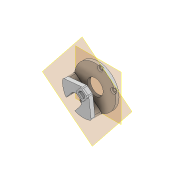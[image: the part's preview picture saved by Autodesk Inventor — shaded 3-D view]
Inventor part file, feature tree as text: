
AUTODESK INVENTOR PART (.ipt)
format: ipt  version: 2022 (Build 260153000, 153)  size: 436,224 bytes
history: native  units: in
note: dims shown in document units (in); Inventor stores cm internally (conversion verified against a paired STEP export)
features: sketch x8, extrude x7, reference x5, projected_geometry x5, other x4, plane x2, fillet x2, hole x1
ambient origin geometry x8: Origin, YZ Plane, XZ Plane, XY Plane, X Axis, Y Axis, Z Axis, Center Point
bodies: Solid1 (feature_tree), Volumenkörper2 (feature_tree)
feature tree (34):
  plane  "Work Plane1"
  extrude  "Extrusion1"  Depth=0.0787in
  hole  "Bohrung1"  [1 undecoded]
  extrude  "Extrusion4"  Depth=0.0787in
  plane  "Arbeitsebene2"
  extrude  "Extrusion6"  Depth=0.2756in TaperAngle=0.0deg
  fillet  "Rundung1"  Radius=0.2651in
  extrude  "Extrusion8"  Depth=0.0787in
  fillet  "Rundung2"  Radius=0.1969in
  extrude  "Extrusion9"  Depth=0.4331in TaperAngle=0.0deg
  extrude  "Extrusion10"  Depth=0.0787in
  extrude  "Extrusion11"  Depth=1.0236in
  sketch  "Sketch1"  dims[d0=0.1575in d1=0.0in]
  reference  "Reference1"
  reference  "Reference5"
  reference  "Reference6"
  reference  "Reference7"
  sketch  "Skizze4"  dims[d9=0.126in d10=0.75in d11=0.2559in d12=0.0787in d13=0.5635in d14=1.0in d15=0.8108in d17=0.7874in]
  reference  "Referenz9"
  sketch  "Skizze6"  dims[d18=0.5118in d19=0.3937in d20=0.0in]
  sketch  "Skizze10"  dims[d33=0.2756in d34=0.0in d37=0.0787in]
  sketch  "Skizze12"  dims[d40=0.5118in d41=0.2756in d42=0.0in d47=0.2651in]
  sketch  "Skizze14"  dims[d48=0.0197in d49=0.0787in d50=0.1969in d51=0.0in]
  projected_geometry  "Projizierte Kontur5"
  projected_geometry  "Projizierte Kontur6"
  projected_geometry  "Projizierte Kontur7"
  sketch  "Skizze16"  dims[d52=0.0in d53=0.4331in d54=0.0in]
  projected_geometry  "Projizierte Kontur8"
  sketch  "Skizze17"  dims[d55=90.0deg d56=0.0787in d57=1.0236in d58=0.0in d59=0.0in]
  projected_geometry  "Projizierte Kontur9"
  other  "<userpath>\Documents\Matchboxscope\INVENTOR\Matchboxscope_v1.iam"
  other  "Matchboxscope_v1.iam"
  other  "Matchboxscope_middle2_v1:1"
  other  "Matchboxscope_middle2_v2:1"
note: 1 required parameter value undecoded (feature->parameter linkage not recoverable at this tier; creation-order binding heuristic only, values carry confidence <= 0.55)
